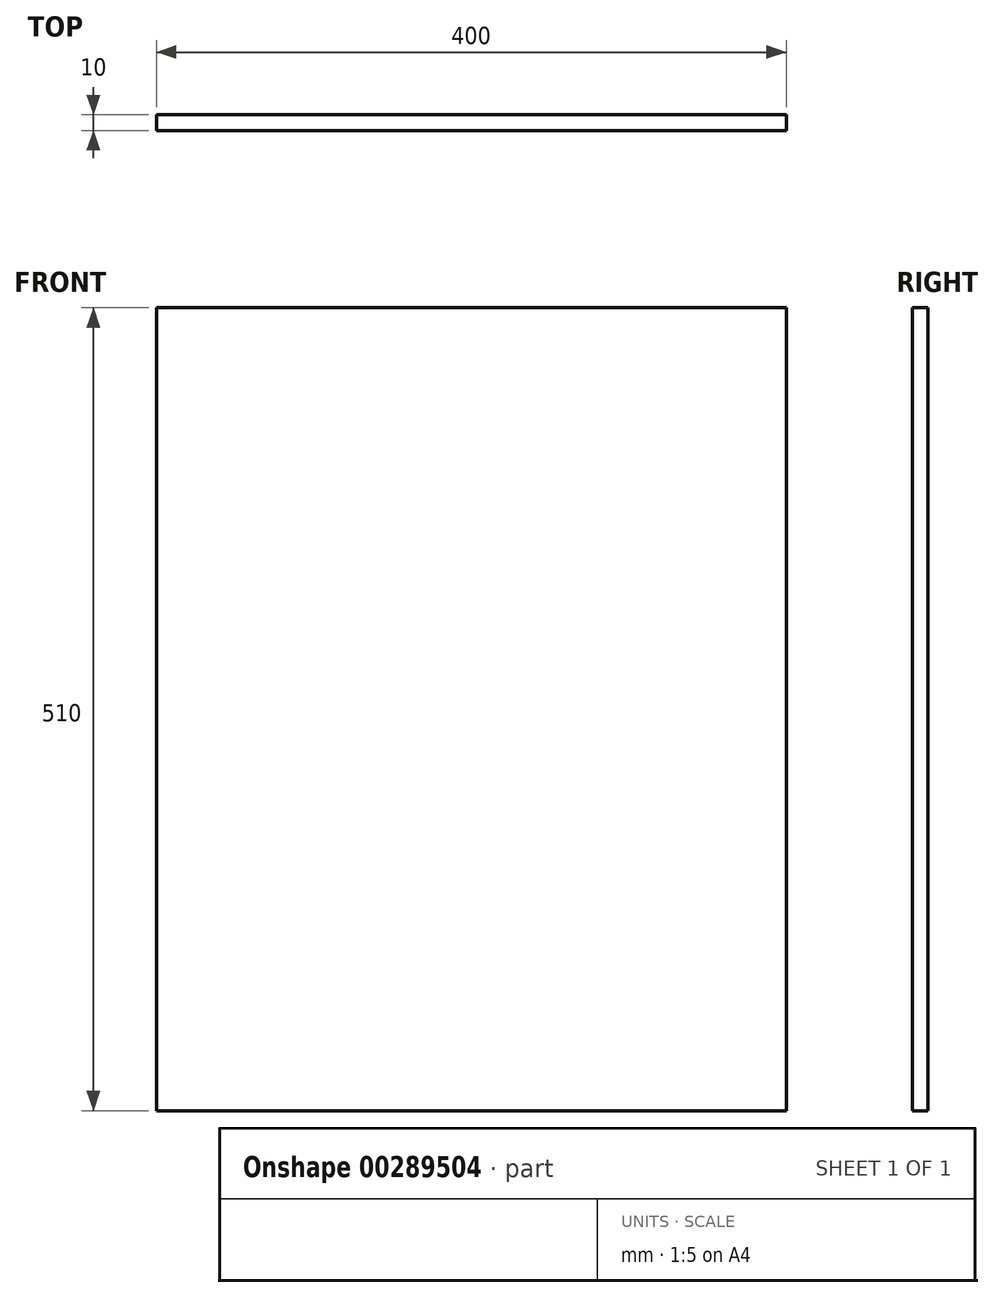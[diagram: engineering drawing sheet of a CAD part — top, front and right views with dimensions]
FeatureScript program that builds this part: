
annotation { "Feature Type Name" : "Feature", "Feature Type Description" : "" }
export const myFeature = defineFeature(function(context is Context, id is Id, definition is map)
    precondition{}
    {
        {
            var Q0;
            Q0=qCreatedBy(makeId("Front.planeOp"),FACE);
            var sketch = newSketch(context, id + "F0", { "sketchPlane" : qUnion([Q0])});
            skLineSegment(sketch, "E0.bottom", {"start": v(200, -255) * mm, "end": v(-200, -255) * mm});
            skLineSegment(sketch, "E0.top", {"start": v(200, 255) * mm, "end": v(-200, 255) * mm});
            skLineSegment(sketch, "E0.left", {"start": v(200, -255) * mm, "end": v(200, 255) * mm});
            skLineSegment(sketch, "E0.right", {"start": v(-200, -255) * mm, "end": v(-200, 255) * mm});
            skPoint(sketch, "E0.middle", {"position": v(0, 0) * mm});
            skSolve(sketch);
        }
        {
            var Q0;
            Q0 = qSketchRegion(id + "F0", true);
            extrude(context, id + "F1", {"entities" : qUnion([Q0]), "depth" : 10 * mm});
        }
    });
